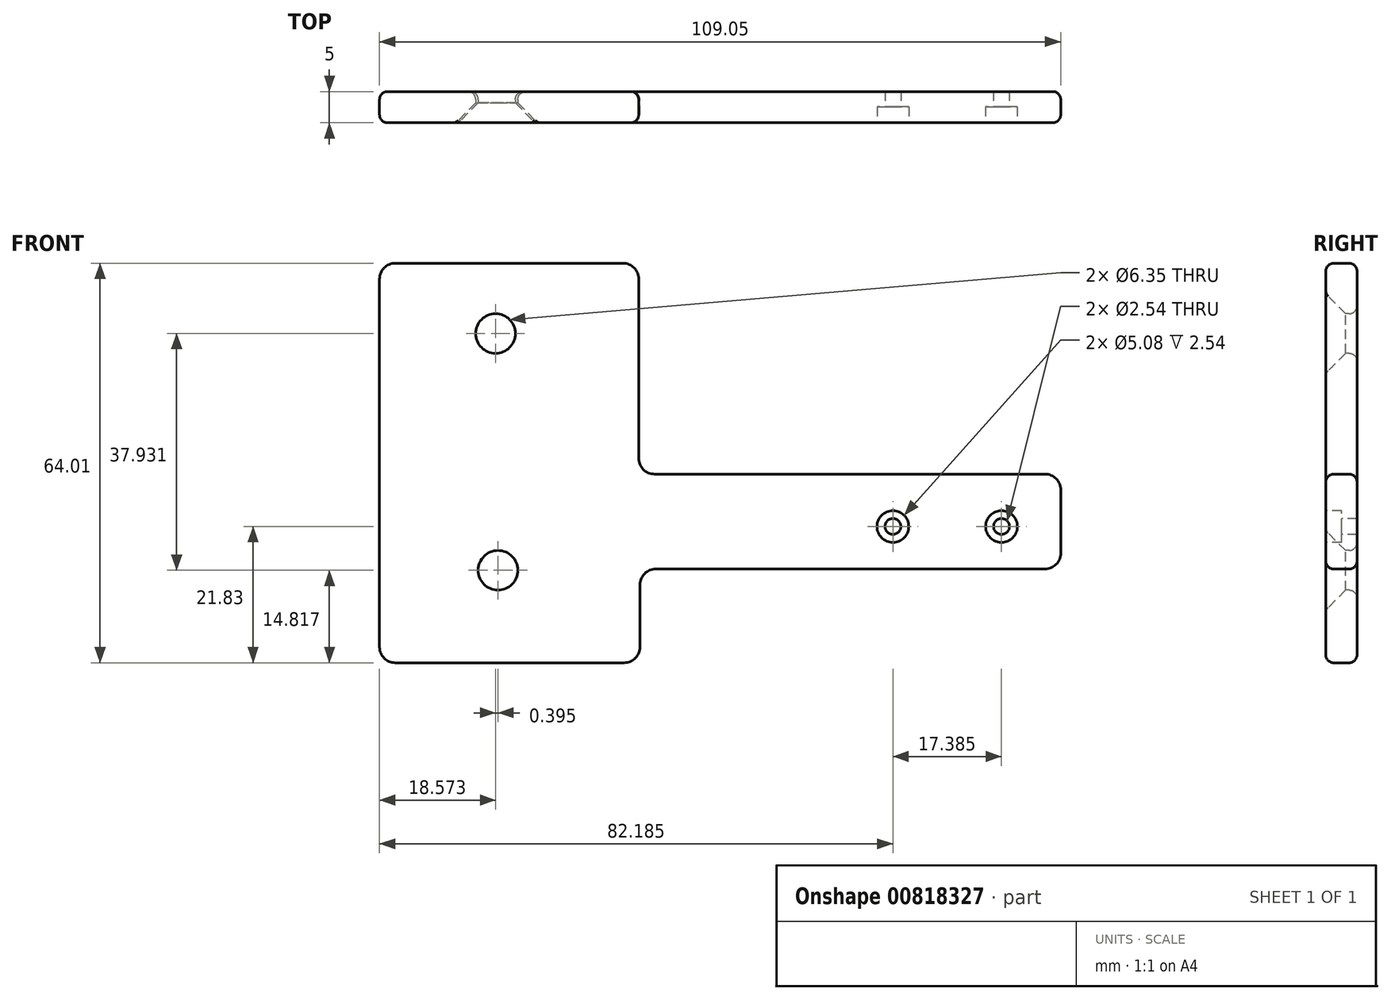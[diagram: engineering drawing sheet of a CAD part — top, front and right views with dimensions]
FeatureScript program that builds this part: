
annotation { "Feature Type Name" : "Feature", "Feature Type Description" : "" }
export const myFeature = defineFeature(function(context is Context, id is Id, definition is map)
    precondition{}
    {
        {
            var Q0;
            Q0=qCreatedBy(makeId("Front.planeOp"),FACE);
            var sketch = newSketch(context, id + "F0", { "sketchPlane" : qUnion([Q0])});
            skLineSegment(sketch, "E0", {"start": v(-58.38, 42.18) * mm, "end": v(-58.38, -21.83) * mm});
            skLineSegment(sketch, "E1", {"start": v(-58.38, -21.83) * mm, "end": v(-16.7, -21.83) * mm});
            skLineSegment(sketch, "E2", {"start": v(-16.7, -21.83) * mm, "end": v(-16.7, -6.82) * mm});
            skLineSegment(sketch, "E3", {"start": v(-16.7, -6.82) * mm, "end": v(50.67, -6.82) * mm});
            skLineSegment(sketch, "E4", {"start": v(50.67, -6.82) * mm, "end": v(50.67, 8.4) * mm});
            skLineSegment(sketch, "E5", {"start": v(50.67, 8.4) * mm, "end": v(-16.9, 8.4) * mm});
            skLineSegment(sketch, "E6", {"start": v(-58.38, 42.18) * mm, "end": v(-16.9, 42.18) * mm});
            skLineSegment(sketch, "E7", {"start": v(-16.9, 8.4) * mm, "end": v(-16.9, 42.18) * mm});
            skSolve(sketch);
        }
        {
            var Q0;
            Q0=makeQuery(id+"F0.imprint","IMPRINT",FACE,{"disambiguationData":[TD([[makeQuery(id+"F0.imprint","IMPRINT",EDGE,{"derivedFrom":sQuery(id+"F0.wireOp",EDGE,"E0")}),1.0]])]});
            extrude(context, id + "F1", {"entities" : qUnion([Q0]), "depth" : 5 * mm, "offsetDistance" : 25.4 * mm});
        }
        {
            var Q0;
            Q0=makeQuery(id+"F1.opExtrude","CAP_FACE",FACE,{"disambiguationData":[OSD([sQuery(id+"F0.wireOp",EDGE,"E0"),sQuery(id+"F0.wireOp",EDGE,"E1"),sQuery(id+"F0.wireOp",EDGE,"E2"),sQuery(id+"F0.wireOp",EDGE,"E3"),sQuery(id+"F0.wireOp",EDGE,"E4"),sQuery(id+"F0.wireOp",EDGE,"E5"),sQuery(id+"F0.wireOp",EDGE,"E6"),sQuery(id+"F0.wireOp",EDGE,"E7")])],"isStart":false});
            var sketch = newSketch(context, id + "F2", { "sketchPlane" : qUnion([Q0])});
            skPoint(sketch, "E8", {"position": v(-39.8, 30.92) * mm});
            skPoint(sketch, "E9", {"position": v(-39.41, -7.01) * mm});
            skPoint(sketch, "E10", {"position": v(23.8, 0) * mm});
            skPoint(sketch, "E11", {"position": v(41.2, 0) * mm});
            skSolve(sketch);
        }
        {
            var Q0;
            Q0=sQuery(id+"F2.wireOp",VERTEX,"E8");
            var Q1;
            Q1=sQuery(id+"F2.wireOp",VERTEX,"E9");
            var Q2;
            Q2=makeQuery(id+"F1.opExtrude","SWEPT_BODY",BODY,{"disambiguationData":[OSD([sQuery(id+"F0.wireOp",EDGE,"E0"),sQuery(id+"F0.wireOp",EDGE,"E1"),sQuery(id+"F0.wireOp",EDGE,"E2"),sQuery(id+"F0.wireOp",EDGE,"E3"),sQuery(id+"F0.wireOp",EDGE,"E4"),sQuery(id+"F0.wireOp",EDGE,"E5"),sQuery(id+"F0.wireOp",EDGE,"E6"),sQuery(id+"F0.wireOp",EDGE,"E7")])]});
            hole(context, id + "F3", {"style" : HoleStyle.C_SINK, "endStyle" : HoleEndStyle.THROUGH, "holeDiameter" : 6.35 * mm, "cSinkDiameter" : 12.7 * mm, "cSinkAngle" : 90 * degree, "majorDiameter" : 6.35 * mm, "isTappedThrough" : true, "tappedDepth" : 12.7 * mm, "tapClearance" : 3, "locations" : qUnion([Q0, Q1]), "scope" : qUnion([Q2])});
        }
        {
            var Q0;
            Q0=makeQuery(id+"F1.opExtrude","SWEPT_EDGE",EDGE,{"disambiguationData":[OSD([sQuery(id+"F0.wireOp",EDGE,"E6"),sQuery(id+"F0.wireOp",EDGE,"E7")])]});
            var Q1;
            Q1=makeQuery(id+"F1.opExtrude","SWEPT_EDGE",EDGE,{"disambiguationData":[OSD([sQuery(id+"F0.wireOp",EDGE,"E0"),sQuery(id+"F0.wireOp",EDGE,"E6")])]});
            var Q2;
            Q2=makeQuery(id+"F1.opExtrude","SWEPT_EDGE",EDGE,{"disambiguationData":[OSD([sQuery(id+"F0.wireOp",EDGE,"E4"),sQuery(id+"F0.wireOp",EDGE,"E5")])]});
            var Q3;
            Q3=makeQuery(id+"F1.opExtrude","SWEPT_EDGE",EDGE,{"disambiguationData":[OSD([sQuery(id+"F0.wireOp",EDGE,"E3"),sQuery(id+"F0.wireOp",EDGE,"E4")])]});
            var Q4;
            Q4=makeQuery(id+"F1.opExtrude","SWEPT_EDGE",EDGE,{"disambiguationData":[OSD([sQuery(id+"F0.wireOp",EDGE,"E1"),sQuery(id+"F0.wireOp",EDGE,"E2")])]});
            var Q5;
            Q5=makeQuery(id+"F1.opExtrude","SWEPT_EDGE",EDGE,{"disambiguationData":[OSD([sQuery(id+"F0.wireOp",EDGE,"E5"),sQuery(id+"F0.wireOp",EDGE,"E7")])]});
            var Q6;
            Q6=makeQuery(id+"F1.opExtrude","SWEPT_EDGE",EDGE,{"disambiguationData":[OSD([sQuery(id+"F0.wireOp",EDGE,"E0"),sQuery(id+"F0.wireOp",EDGE,"E1")])]});
            var Q7;
            Q7=makeQuery(id+"F1.opExtrude","SWEPT_EDGE",EDGE,{"disambiguationData":[OSD([sQuery(id+"F0.wireOp",EDGE,"E2"),sQuery(id+"F0.wireOp",EDGE,"E3")])]});
            fillet(context, id + "F4", {"entities" : qUnion([Q0, Q1, Q2, Q3, Q4, Q5, Q6, Q7]), "radius" : 2.54 * mm, "tangentPropagation" : true, "allowEdgeOverflow" : false});
        }
        {
            var Q0;
            Q0=makeQuery(id+"F1.opExtrude","CAP_FACE",FACE,{"disambiguationData":[OSD([sQuery(id+"F0.wireOp",EDGE,"E0"),sQuery(id+"F0.wireOp",EDGE,"E1"),sQuery(id+"F0.wireOp",EDGE,"E2"),sQuery(id+"F0.wireOp",EDGE,"E3"),sQuery(id+"F0.wireOp",EDGE,"E4"),sQuery(id+"F0.wireOp",EDGE,"E5"),sQuery(id+"F0.wireOp",EDGE,"E6"),sQuery(id+"F0.wireOp",EDGE,"E7")])],"isStart":true});
            var Q1;
            Q1=makeQuery(id+"F1.opExtrude","CAP_FACE",FACE,{"disambiguationData":[OSD([sQuery(id+"F0.wireOp",EDGE,"E0"),sQuery(id+"F0.wireOp",EDGE,"E1"),sQuery(id+"F0.wireOp",EDGE,"E2"),sQuery(id+"F0.wireOp",EDGE,"E3"),sQuery(id+"F0.wireOp",EDGE,"E4"),sQuery(id+"F0.wireOp",EDGE,"E5"),sQuery(id+"F0.wireOp",EDGE,"E6"),sQuery(id+"F0.wireOp",EDGE,"E7")])],"isStart":false});
            fillet(context, id + "F5", {"entities" : qUnion([Q0, Q1]), "radius" : 1.27 * mm, "tangentPropagation" : true, "allowEdgeOverflow" : false});
        }
        {
            var Q0;
            Q0=sQuery(id+"F2.wireOp",VERTEX,"E10");
            var Q1;
            Q1=sQuery(id+"F2.wireOp",VERTEX,"E11");
            var Q2;
            Q2=makeQuery(id+"F1.opExtrude","SWEPT_BODY",BODY,{"disambiguationData":[OSD([sQuery(id+"F0.wireOp",EDGE,"E0"),sQuery(id+"F0.wireOp",EDGE,"E1"),sQuery(id+"F0.wireOp",EDGE,"E2"),sQuery(id+"F0.wireOp",EDGE,"E3"),sQuery(id+"F0.wireOp",EDGE,"E4"),sQuery(id+"F0.wireOp",EDGE,"E5"),sQuery(id+"F0.wireOp",EDGE,"E6"),sQuery(id+"F0.wireOp",EDGE,"E7")])]});
            hole(context, id + "F6", {"style" : HoleStyle.C_BORE, "endStyle" : HoleEndStyle.THROUGH, "holeDiameter" : 2.54 * mm, "cBoreDiameter" : 5.08 * mm, "cBoreDepth" : 2.54 * mm, "majorDiameter" : 6.35 * mm, "isTappedThrough" : true, "tappedDepth" : 12.7 * mm, "tapClearance" : 3, "startFromSketch" : true, "locations" : qUnion([Q0, Q1]), "scope" : qUnion([Q2])});
        }
    });
